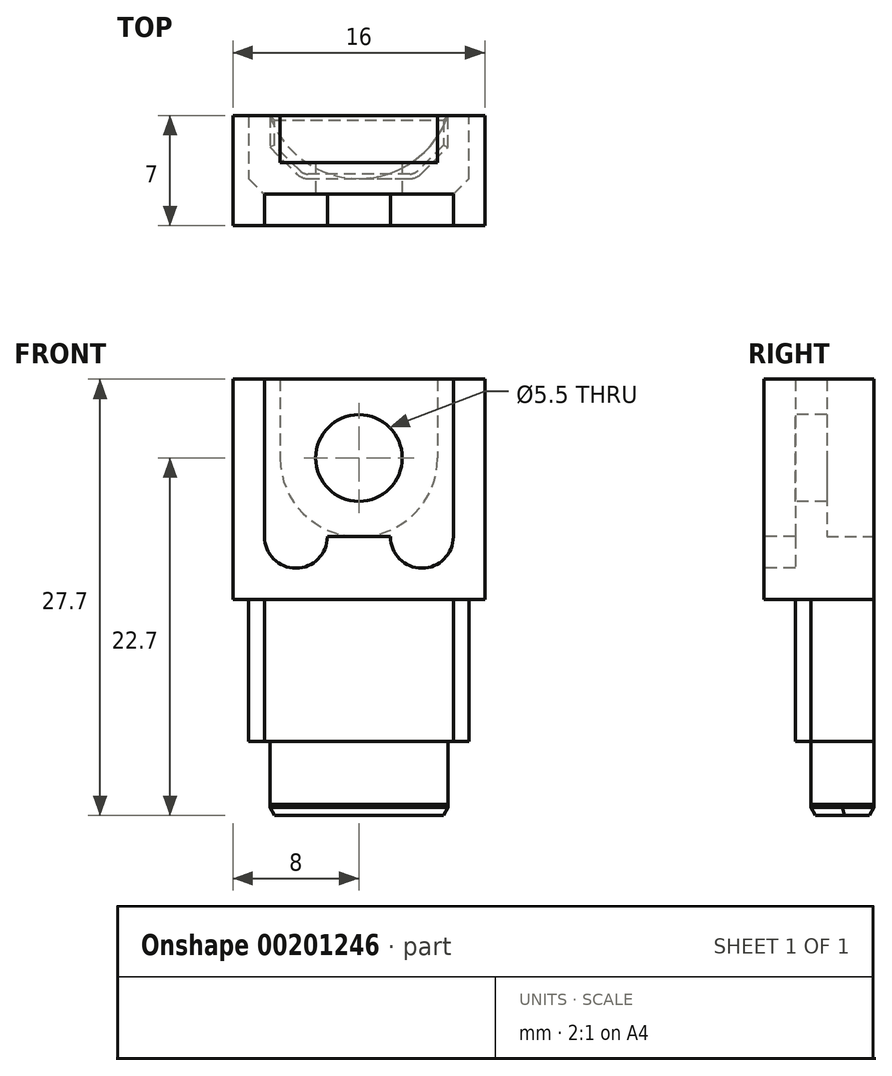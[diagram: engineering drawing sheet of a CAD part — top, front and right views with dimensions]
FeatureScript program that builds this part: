
annotation { "Feature Type Name" : "Feature", "Feature Type Description" : "" }
export const myFeature = defineFeature(function(context is Context, id is Id, definition is map)
    precondition{}
    {
        {
            var Q0;
            Q0=qCreatedBy(makeId("Top.planeOp"),FACE);
            var sketch = newSketch(context, id + "F0", { "sketchPlane" : qUnion([Q0])});
            skLineSegment(sketch, "E0.bottom", {"start": v(-8, 0) * mm, "end": v(8, 0) * mm});
            skLineSegment(sketch, "E0.top", {"start": v(-8, -7) * mm, "end": v(8, -7) * mm});
            skLineSegment(sketch, "E0.left", {"start": v(-8, 0) * mm, "end": v(-8, -7) * mm});
            skLineSegment(sketch, "E0.right", {"start": v(8, 0) * mm, "end": v(8, -7) * mm});
            skLineSegment(sketch, "E1", {"start": v(-7, 0) * mm, "end": v(-7, -4) * mm});
            skLineSegment(sketch, "E2", {"start": v(-7, -4) * mm, "end": v(-6, -5) * mm});
            skLineSegment(sketch, "E3", {"start": v(-6, -5) * mm, "end": v(6, -5) * mm});
            skLineSegment(sketch, "E4", {"start": v(6, -5) * mm, "end": v(7, -4) * mm});
            skLineSegment(sketch, "E5", {"start": v(7, -4) * mm, "end": v(7, 0) * mm});
            skLineSegment(sketch, "E6", {"start": v(-5.66, 0) * mm, "end": v(-5.66, -2) * mm});
            skLineSegment(sketch, "E7", {"start": v(-5.66, -2) * mm, "end": v(-3.95, -3.7) * mm});
            skLineSegment(sketch, "E8", {"start": v(-3.24, -4) * mm, "end": v(3.24, -4) * mm});
            skLineSegment(sketch, "E9", {"start": v(3.95, -3.7) * mm, "end": v(5.66, -2) * mm});
            skLineSegment(sketch, "E10", {"start": v(5.66, -2) * mm, "end": v(5.66, 0) * mm});
            skPoint(sketch, "E11.visualSharp", {"position": v(-3.66, -4) * mm});
            skArc(sketch, "E11.filletArc", {"start": v(-3.95, -3.7) * mm, "mid": v(-3.63, -3.92) * mm, "end": v(-3.24, -4) * mm});
            skPoint(sketch, "E12.visualSharp", {"position": v(3.66, -4) * mm});
            skArc(sketch, "E12.filletArc", {"start": v(3.24, -4) * mm, "mid": v(3.63, -3.92) * mm, "end": v(3.95, -3.7) * mm});
            skArc(sketch, "E13", {"start": v(-5.66, 0) * mm, "mid": v(0, -4) * mm, "end": v(5.66, 0) * mm});
            skSolve(sketch);
        }
        {
            var Q0;
            {var subQ0=sQuery(id+"F0.wireOp",EDGE,"E13");var subQ4=makeQuery(id+"F0.imprint","INTERSECT",VERTEX,{"derivedFrom":[sQuery(id+"F0.wireOp",EDGE,"E8"),subQ0]});Q0=makeQuery(id+"F0.imprint","IMPRINT",FACE,{"disambiguationData":[TD([[makeQuery(id+"F0.imprint","IMPRINT",EDGE,{"disambiguationData":[TD([[subQ4,1.0]])],"derivedFrom":subQ0}),1.0]])]});}
            var Q1;
            {var subQ4=sQuery(id+"F0.wireOp",EDGE,"E6");Q1=makeQuery(id+"F0.imprint","IMPRINT",FACE,{"disambiguationData":[TD([[makeQuery(id+"F0.imprint","IMPRINT",EDGE,{"derivedFrom":subQ4}),1.0]])]});}
            var Q2;
            Q2=makeQuery(id+"F0.imprint","IMPRINT",FACE,{"disambiguationData":[TD([[makeQuery(id+"F0.imprint","IMPRINT",EDGE,{"derivedFrom":sQuery(id+"F0.wireOp",EDGE,"E9")}),1.0]])]});
            extrude(context, id + "F1", {"entities" : qUnion([Q0, Q1, Q2]), "depth" : 0.7 * mm});
        }
        {
            var Q0;
            Q0=makeQuery(id+"F1.opExtrude","CAP_FACE",FACE,{"disambiguationData":[OSD([sQuery(id+"F0.wireOp",EDGE,"E0.bottom"),sQuery(id+"F0.wireOp",EDGE,"E6"),sQuery(id+"F0.wireOp",EDGE,"E7"),sQuery(id+"F0.wireOp",EDGE,"E8"),sQuery(id+"F0.wireOp",EDGE,"E9"),sQuery(id+"F0.wireOp",EDGE,"E10"),sQuery(id+"F0.wireOp",EDGE,"E11.filletArc"),sQuery(id+"F0.wireOp",EDGE,"E12.filletArc")])],"isStart":false});
            var sketch = newSketch(context, id + "F2", { "sketchPlane" : qUnion([Q0])});
            skArc(sketch, "E14.0", {"start": v(-5.66, 0) * mm, "mid": v(0, -4) * mm, "end": v(5.66, 0) * mm});
            skLineSegment(sketch, "E15.0", {"start": v(-8, 0) * mm, "end": v(8, 0) * mm});
            skSolve(sketch);
        }
        {
            var Q0;
            {var subQ0=sQuery(id+"F2.wireOp",EDGE,"E14.0");var subQ4=makeQuery(id+"F2.imprint","INTERSECT",VERTEX,{"derivedFrom":[makeQuery(id+"F1.opExtrude","CAP_EDGE",EDGE,{"disambiguationData":[OSD([sQuery(id+"F0.wireOp",EDGE,"E8")])],"isStart":false}),subQ0]});Q0=makeQuery(id+"F2.imprint","IMPRINT",FACE,{"disambiguationData":[TD([[makeQuery(id+"F2.imprint","IMPRINT",EDGE,{"disambiguationData":[TD([[subQ4,1.0]])],"derivedFrom":subQ0}),1.0]])]});}
            extrude(context, id + "F3", {"entities" : qUnion([Q0]), "operationType" : NewBodyOperationType.ADD, "depth" : 4 * mm});
        }
        {
            var Q0;
            Q0=makeQuery(id+"F3.opExtrude","CAP_FACE",FACE,{"disambiguationData":[OSD([sQuery(id+"F0.wireOp",EDGE,"E8"),sQuery(id+"F2.wireOp",EDGE,"E14.0"),sQuery(id+"F2.wireOp",EDGE,"E15.0")])],"isStart":false});
            var sketch = newSketch(context, id + "F4", { "sketchPlane" : qUnion([Q0])});
            skLineSegment(sketch, "E16.0", {"start": v(-8, 0) * mm, "end": v(8, 0) * mm});
            skLineSegment(sketch, "E17.0", {"start": v(-7, 0) * mm, "end": v(-7, -4) * mm});
            skLineSegment(sketch, "E18.0", {"start": v(-7, -4) * mm, "end": v(-6, -5) * mm});
            skLineSegment(sketch, "E19.0", {"start": v(-6, -5) * mm, "end": v(6, -5) * mm});
            skLineSegment(sketch, "E20.0", {"start": v(6, -5) * mm, "end": v(7, -4) * mm});
            skLineSegment(sketch, "E21.0", {"start": v(7, -4) * mm, "end": v(7, 0) * mm});
            skSolve(sketch);
        }
        {
            var Q0;
            {var subQ3=sQuery(id+"F0.wireOp",EDGE,"E8");Q0=makeQuery(id+"F4.imprint","IMPRINT",FACE,{"disambiguationData":[TD([[makeQuery(id+"F4.imprint","IMPRINT",EDGE,{"derivedFrom":makeQuery(id+"F3.opExtrude","CAP_EDGE",EDGE,{"disambiguationData":[OSD([subQ3])],"isStart":false})}),1.0]])]});}
            var Q1;
            {var subQ0=sQuery(id+"F4.wireOp",EDGE,"E17.0");Q1=makeQuery(id+"F4.imprint","IMPRINT",FACE,{"disambiguationData":[TD([[makeQuery(id+"F4.imprint","IMPRINT",EDGE,{"derivedFrom":subQ0}),1.0]])]});}
            var Q2;
            {var subQ1=makeQuery(id+"F3.opExtrude","CAP_EDGE",EDGE,{"disambiguationData":[OSD([sQuery(id+"F2.wireOp",EDGE,"E14.0")])],"isStart":false});Q2=makeQuery(id+"F4.imprint","IMPRINT",FACE,{"disambiguationData":[TD([[makeQuery(id+"F4.imprint","IMPRINT",EDGE,{"derivedFrom":subQ1}),1.0]])]});}
            extrude(context, id + "F5", {"entities" : qUnion([Q0, Q1, Q2]), "operationType" : NewBodyOperationType.ADD, "depth" : (13.7 - 4.7) * mm});
        }
        {
            var Q0;
            Q0=makeQuery(id+"F5.opExtrude","CAP_FACE",FACE,{"disambiguationData":[OSD([sQuery(id+"F4.wireOp",EDGE,"E16.0"),sQuery(id+"F4.wireOp",EDGE,"E17.0"),sQuery(id+"F4.wireOp",EDGE,"E18.0"),sQuery(id+"F4.wireOp",EDGE,"E19.0"),sQuery(id+"F4.wireOp",EDGE,"E20.0"),sQuery(id+"F4.wireOp",EDGE,"E21.0")])],"isStart":false});
            var sketch = newSketch(context, id + "F6", { "sketchPlane" : qUnion([Q0])});
            skLineSegment(sketch, "E22.0", {"start": v(-8, 0) * mm, "end": v(-8, -7) * mm});
            skLineSegment(sketch, "E23.0", {"start": v(-8, -7) * mm, "end": v(8, -7) * mm});
            skLineSegment(sketch, "E24.0", {"start": v(8, 0) * mm, "end": v(8, -7) * mm});
            skLineSegment(sketch, "E25.0", {"start": v(-8, 0) * mm, "end": v(8, 0) * mm});
            skSolve(sketch);
        }
        {
            var Q0;
            Q0 = qSketchRegion(id + "F6", true);
            extrude(context, id + "F7", {"entities" : qUnion([Q0]), "operationType" : NewBodyOperationType.ADD, "depth" : (27.7 - 13.7) * mm});
        }
        {
            var Q0;
            Q0=makeQuery(id+"F7.opExtrude","SWEPT_FACE",FACE,{"disambiguationData":[OSD([sQuery(id+"F6.wireOp",EDGE,"E23.0")])]});
            var sketch = newSketch(context, id + "F8", { "sketchPlane" : qUnion([Q0])});
            skLineSegment(sketch, "E26", {"start": v(0, 27.7) * mm, "end": v(0, 13.7) * mm, "construction": true});
            skCircle(sketch, "E27", {"center": v(0, 22.7) * mm, "radius": 2.75 * mm});
            skSolve(sketch);
        }
        {
            var Q0;
            Q0 = qSketchRegion(id + "F8", true);
            extrude(context, id + "F9", {"entities" : qUnion([Q0]), "operationType" : NewBodyOperationType.REMOVE, "endBound" : BoundingType.THROUGH_ALL, "oppositeDirection" : true, "depth" : 25 * mm});
        }
        {
            var Q0;
            Q0=makeQuery(id+"F7.opExtrude","SWEPT_FACE",FACE,{"disambiguationData":[OSD([sQuery(id+"F6.wireOp",EDGE,"E23.0")])]});
            var sketch = newSketch(context, id + "F10", { "sketchPlane" : qUnion([Q0])});
            skLineSegment(sketch, "E28", {"start": v(0, 27.7) * mm, "end": v(0, 13.7) * mm, "construction": true});
            skLineSegment(sketch, "E29", {"start": v(-6, 27.7) * mm, "end": v(-6, 17.7) * mm});
            skLineSegment(sketch, "E30", {"start": v(6, 27.7) * mm, "end": v(6, 17.7) * mm});
            skLineSegment(sketch, "E31", {"start": v(-2, 17.7) * mm, "end": v(2, 17.7) * mm});
            skArc(sketch, "E32", {"start": v(-6, 17.7) * mm, "mid": v(-4, 15.7) * mm, "end": v(-2, 17.7) * mm});
            skArc(sketch, "E33", {"start": v(2, 17.7) * mm, "mid": v(4, 15.7) * mm, "end": v(6, 17.7) * mm});
            skSolve(sketch);
        }
        {
            var Q0;
            {var subQ1=sQuery(id+"F10.wireOp",EDGE,"E29");Q0=makeQuery(id+"F10.imprint","IMPRINT",FACE,{"disambiguationData":[TD([[makeQuery(id+"F10.imprint","IMPRINT",EDGE,{"derivedFrom":subQ1}),1.0]])]});}
            extrude(context, id + "F11", {"entities" : qUnion([Q0]), "operationType" : NewBodyOperationType.REMOVE, "oppositeDirection" : true, "depth" : 2 * mm});
        }
        {
            var Q0;
            Q0=makeQuery(id+"F7.boolean.opBoolean","MERGE",FACE,{"derivedFrom":[makeQuery(id+"F5.boolean.opBoolean","MERGE",FACE,{"derivedFrom":[makeQuery(id+"F3.boolean.opBoolean","MERGE",FACE,{"derivedFrom":[makeQuery(id+"F1.opExtrude","SWEPT_FACE",FACE,{"disambiguationData":[OSD([sQuery(id+"F0.wireOp",EDGE,"E0.bottom")])]}),makeQuery(id+"F3.opExtrude","SWEPT_FACE",FACE,{"disambiguationData":[OSD([sQuery(id+"F2.wireOp",EDGE,"E15.0")])]})]}),makeQuery(id+"F5.opExtrude","SWEPT_FACE",FACE,{"disambiguationData":[OSD([sQuery(id+"F4.wireOp",EDGE,"E16.0")])]})]}),makeQuery(id+"F7.opExtrude","SWEPT_FACE",FACE,{"disambiguationData":[OSD([sQuery(id+"F6.wireOp",EDGE,"E25.0")])]})]});
            var sketch = newSketch(context, id + "F12", { "sketchPlane" : qUnion([Q0])});
            skLineSegment(sketch, "E34", {"start": v(0, 27.7) * mm, "end": v(0, 0) * mm, "construction": true});
            skLineSegment(sketch, "E35", {"start": v(-5, 27.7) * mm, "end": v(-5, 22.7) * mm});
            skLineSegment(sketch, "E36", {"start": v(5, 27.7) * mm, "end": v(5, 22.7) * mm});
            skArc(sketch, "E37", {"start": v(-5, 22.7) * mm, "mid": v(0, 17.7) * mm, "end": v(5, 22.7) * mm});
            skSolve(sketch);
        }
        {
            var Q0;
            {var subQ2=sQuery(id+"F12.wireOp",EDGE,"E35");Q0=makeQuery(id+"F12.imprint","IMPRINT",FACE,{"disambiguationData":[TD([[makeQuery(id+"F12.imprint","IMPRINT",EDGE,{"derivedFrom":subQ2}),1.0]])]});}
            extrude(context, id + "F13", {"entities" : qUnion([Q0]), "operationType" : NewBodyOperationType.REMOVE, "oppositeDirection" : true, "depth" : 3 * mm});
        }
        {
            var Q0;
            Q0=makeQuery(id+"F1.opExtrude","CAP_FACE",FACE,{"disambiguationData":[OSD([sQuery(id+"F0.wireOp",EDGE,"E0.bottom"),sQuery(id+"F0.wireOp",EDGE,"E6"),sQuery(id+"F0.wireOp",EDGE,"E7"),sQuery(id+"F0.wireOp",EDGE,"E8"),sQuery(id+"F0.wireOp",EDGE,"E9"),sQuery(id+"F0.wireOp",EDGE,"E10"),sQuery(id+"F0.wireOp",EDGE,"E11.filletArc"),sQuery(id+"F0.wireOp",EDGE,"E12.filletArc")])],"isStart":true});
            chamfer(context, id + "F14", {"entities" : qUnion([Q0]), "chamferType" : ChamferType.OFFSET_ANGLE, "width" : 0.5 * mm, "oppositeDirection" : true, "angle" : 30 * degree, "tangentPropagation" : true});
        }
    });
